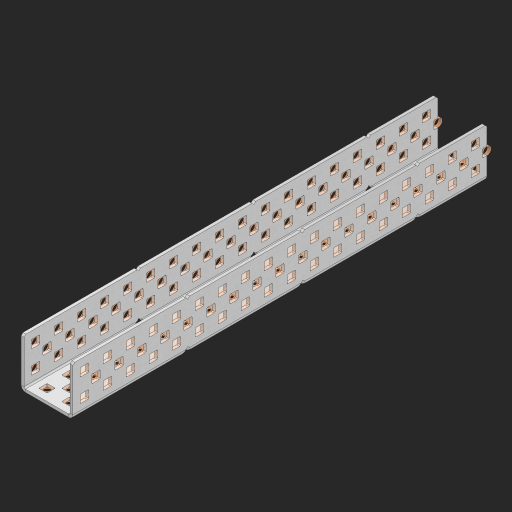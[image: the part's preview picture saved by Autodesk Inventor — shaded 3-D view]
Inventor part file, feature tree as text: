
AUTODESK INVENTOR PART (.ipt)
format: ipt  version: 2023 (Build 270158000, 158)  size: 2,102,784 bytes
history: native  units: in
note: dims shown in document units (in); Inventor stores cm internally (conversion verified against a paired STEP export)
features: other x222, extrude x214, sheet_metal_op x8, sketch x7, mirror x3, pattern_linear x2, chamfer x1
ambient origin geometry x8: Origin, YZ Plane, XZ Plane, XY Plane, X Axis, Y Axis, Z Axis, Center Point
bodies: Solid1 (feature_tree), Body (feature_tree)
feature tree (457):
  sheet_metal_op  "Flanges"
  sheet_metal_op  "Body Pattern"
  pattern_linear  "Center Pattern"  Spacing1=1.0in  [1 undecoded]
  other  "Arc Length"
  mirror  "Notch Mirror"
  pattern_linear  "Notch Pattern"  Spacing1=0.25in  [1 undecoded]
  other  "Diagonal Plane"
  mirror  "Flange 1"
  mirror  "Flange 2"
  chamfer  "End Chamfer"
  sketch  "Sketch1"  dims[d0=1.0in]
  other  "Plate1"
  sketch  "Sketch2"  dims[d1=9.0in]
  other  "Plate2"
  sheet_metal_op  "Bend1"
  sheet_metal_op  "Corner1"
  sketch  "Sketch8"  dims[d2=0.0625in]
  sketch  "Sketch9"  dims[d3=0.0625in]
  other  "Srf91"
  sheet_metal_op  "Body Pattern Sketch"
  other  "Srf92"
  sketch  "Sketch13"  dims[d4=0.0312in]
  sketch  "Sketch15"  dims[d5=0.125in]
  sketch  "Sketch16"  dims[d6=0.0625in d7=1.0in d8=90.0deg d9=0.0312in d10=0.25in d11=0.0625in d12=0.0625in d49=0.182in d50=0.02in d52=0.25in d53=0.0625in d54=0.0in d55=0.172in d56=1.0in d57=0.0in d60=7.0866in d62=0.5in d63=0.7874in d65=0.5in d85=0.1473in d86=0.1782in d88=0.04in d89=0.0625in d90=0.0in d91=0.04in d92=0.0491in d95=2.5in d96=0.04in d97=0.25in d98=45.0deg d99=0.25in d102=2.497in d106=0.182in d107=0.02in d108=0.5in d110=0.0625in d111=0.0in d112=0.172in d113=0.5in d114=0.0in d117=0.5in d118=0.5in d131=0.25in d132=0.25in]
  other  "Srf786"
  other  "Srf889"
  other  "Srf890"
  other  "Srf891"
  other  "Srf892"
  other  "Srf893"
  other  "Srf894"
  other  "Srf895"
  other  "Srf896"
  other  "Srf996"
  other  "Srf997"
  other  "Srf998"
  other  "Srf999"
  other  "Srf1000"
  other  "Srf1255"
  other  "Srf1256"
  other  "Srf1257"
  other  "Srf1258"
  other  "Srf1315"
  other  "Srf1316"
  other  "Srf1317"
  other  "Srf1325"
  other  "Srf1326"
  other  "Srf1327"
  other  "Srf1328"
  other  "Srf1329"
  other  "Srf1330"
  other  "Srf1331"
  other  "Srf1332"
  other  "Srf1338"
  other  "Srf1339"
  other  "Srf1340"
  other  "Srf1341"
  other  "Srf1342"
  other  "Srf1369"
  other  "Srf1370"
  other  "Srf1371"
  other  "Srf1372"
  other  "Srf1374"
  other  "Srf1375"
  other  "Srf1376"
  other  "Srf1384"
  other  "Srf1385"
  other  "Srf1386"
  other  "Srf1387"
  other  "Srf1388"
  other  "Srf1389"
  other  "Srf1390"
  other  "Srf1391"
  other  "Srf1397"
  other  "Srf1398"
  other  "Srf1399"
  other  "Srf1400"
  other  "Srf1401"
  other  "Srf1428"
  other  "Srf1429"
  other  "Srf1430"
  other  "Srf1431"
  other  "Srf1433"
  other  "Srf1434"
  other  "Srf1473"
  other  "Srf1474"
  other  "Srf1475"
  other  "Srf1476"
  other  "Srf1477"
  other  "Srf1478"
  other  "Srf1479"
  other  "Srf1480"
  other  "Srf1481"
  other  "Srf1482"
  other  "Srf1483"
  other  "Srf1484"
  other  "Srf1485"
  other  "Srf1486"
  other  "Srf1487"
  other  "Srf1488"
  other  "Srf1489"
  other  "Srf1490"
  other  "Srf1500"
  other  "Srf1501"
  other  "Srf1502"
  other  "Srf1503"
  other  "Srf1504"
  other  "Srf1505"
  other  "Srf1506"
  other  "Srf1507"
  other  "Srf1508"
  other  "Srf1509"
  other  "Srf1510"
  other  "Srf1511"
  other  "Srf1512"
  other  "Srf1513"
  other  "Srf1514"
  other  "Srf1515"
  other  "Srf1516"
  other  "Srf1517"
  other  "Srf1518"
  other  "Srf1519"
  other  "Srf1520"
  other  "Srf1521"
  other  "Srf1522"
  other  "Srf1523"
  other  "Srf1524"
  other  "Srf1525"
  other  "Srf1526"
  other  "Srf1527"
  other  "Srf1528"
  other  "Srf1529"
  other  "Srf1530"
  other  "Srf1531"
  other  "Srf1532"
  other  "Srf1533"
  other  "Srf1538"
  other  "Srf1539"
  other  "Srf1540"
  other  "Srf1541"
  other  "Srf1542"
  other  "Srf1543"
  other  "Srf1544"
  other  "Srf1545"
  other  "Srf1546"
  other  "Srf1547"
  other  "Srf1548"
  other  "Srf1549"
  other  "Srf1550"
  other  "Srf1551"
  other  "Srf1552"
  other  "Srf1553"
  other  "Srf1554"
  other  "Srf1555"
  other  "Srf1556"
  other  "Srf1557"
  other  "Srf1558"
  other  "Srf1559"
  other  "Srf1560"
  other  "Srf1561"
  other  "Srf1562"
  other  "Srf1563"
  other  "Srf1564"
  other  "Srf1565"
  other  "Srf1566"
  other  "Srf1567"
  other  "Srf1568"
  other  "Srf1569"
  other  "Srf1570"
  other  "Srf1571"
  other  "Srf1576"
  other  "Srf1577"
  other  "Srf1578"
  other  "Srf1579"
  other  "Srf1580"
  other  "Srf1581"
  other  "Srf1582"
  other  "Srf1583"
  other  "Srf1584"
  other  "Srf1585"
  other  "Srf1586"
  other  "Srf1587"
  other  "Srf1588"
  other  "Srf1589"
  other  "Srf1590"
  other  "Srf1591"
  other  "Srf1592"
  other  "Srf1593"
  other  "Srf1594"
  other  "Srf1595"
  other  "Srf1596"
  other  "Srf1597"
  other  "Srf1598"
  other  "Srf1599"
  other  "Srf1600"
  other  "Srf1601"
  other  "Srf1602"
  other  "Srf1603"
  other  "Srf1604"
  other  "Srf1605"
  other  "Srf1606"
  other  "Srf1607"
  other  "Srf1608"
  other  "Srf1609"
  other  "Srf1614"
  other  "Srf1615"
  other  "Srf1616"
  other  "Srf1617"
  other  "Srf1618"
  other  "Srf1619"
  other  "Srf1620"
  other  "Srf1621"
  other  "Srf1622"
  other  "Srf1623"
  other  "Srf1624"
  other  "Srf1625"
  other  "Srf1626"
  other  "Srf1627"
  other  "Srf1628"
  other  "Srf1629"
  other  "Srf1630"
  other  "Srf1631"
  other  "Srf1632"
  other  "Srf1633"
  other  "Srf1634"
  other  "Srf1635"
  other  "Srf1636"
  other  "Srf1637"
  other  "Srf1638"
  other  "Srf1639"
  other  "Srf1640"
  other  "Srf1641"
  other  "Srf1642"
  other  "Srf1643"
  other  "Srf1644"
  other  "Srf1645"
  other  "Srf1646"
  other  "Srf1647"
  sheet_metal_op  "Body Stamp"
  sheet_metal_op  "Body Circle"
  other  "Center Stamp"
  other  "Center Circle"
  sheet_metal_op  "Notch"
  extrude  "ExtrusionSrf92"  Depth=0.0625in
  extrude  "ExtrusionSrf889"  Depth=0.0625in
  extrude  "ExtrusionSrf890"  Depth=0.182in
  extrude  "ExtrusionSrf891"  Depth=0.02in
  extrude  "ExtrusionSrf892"  Depth=0.25in
  extrude  "ExtrusionSrf893"  Depth=0.0625in
  extrude  "ExtrusionSrf894"  TaperAngle=0.0deg  [1 undecoded]
  extrude  "ExtrusionSrf895"  Depth=0.25in
  extrude  "ExtrusionSrf896"  Depth=1.0in TaperAngle=0.0deg
  extrude  "ExtrusionSrf996"  Depth=0.25in
  extrude  "ExtrusionSrf997"  Depth=0.5in
  extrude  "ExtrusionSrf998"  Depth=0.25in
  extrude  "ExtrusionSrf999"  Depth=0.25in
  extrude  "ExtrusionSrf1000"  Depth=0.25in
  extrude  "ExtrusionSrf1255"  Depth=0.0625in
  extrude  "ExtrusionSrf1256"  TaperAngle=0.0deg  [1 undecoded]
  extrude  "ExtrusionSrf1257"  Depth=0.25in
  extrude  "ExtrusionSrf1258"  Depth=0.25in
  extrude  "ExtrusionSrf1315"  Depth=2.5in
  extrude  "ExtrusionSrf1316"  Depth=0.25in TaperAngle=45.0deg
  extrude  "ExtrusionSrf1355"  Depth=0.25in
  extrude  "ExtrusionSrf1356"  Depth=0.25in
  extrude  "ExtrusionSrf1357"  Depth=0.182in
  extrude  "ExtrusionSrf1358"  Depth=0.02in
  extrude  "ExtrusionSrf1359"  Depth=0.5in
  extrude  "ExtrusionSrf1360"  Depth=0.0625in
  extrude  "ExtrusionSrf1361"  TaperAngle=0.0deg  [1 undecoded]
  extrude  "ExtrusionSrf1362"  Depth=0.25in
  extrude  "ExtrusionSrf1363"  Depth=0.5in TaperAngle=0.0deg
  extrude  "ExtrusionSrf1364"  Depth=0.5in
  extrude  "ExtrusionSrf1365"  Depth=0.5in
  extrude  "ExtrusionSrf1366"  Depth=0.25in
  extrude  "ExtrusionSrf1367"  Depth=0.25in
  extrude  "ExtrusionSrf1368"  [1 undecoded]
  extrude  "ExtrusionSrf1369"  [1 undecoded]
  extrude  "ExtrusionSrf1370"  [1 undecoded]
  extrude  "ExtrusionSrf1371"  [1 undecoded]
  extrude  "ExtrusionSrf1372"  [1 undecoded]
  extrude  "ExtrusionSrf1374"  [1 undecoded]
  extrude  "ExtrusionSrf1375"  [1 undecoded]
  extrude  "ExtrusionSrf1414"  [1 undecoded]
  extrude  "ExtrusionSrf1415"  [1 undecoded]
  extrude  "ExtrusionSrf1416"  [1 undecoded]
  extrude  "ExtrusionSrf1417"  [1 undecoded]
  extrude  "ExtrusionSrf1418"  [1 undecoded]
  extrude  "ExtrusionSrf1419"  [1 undecoded]
  extrude  "ExtrusionSrf1420"  [1 undecoded]
  extrude  "ExtrusionSrf1421"  [1 undecoded]
  extrude  "ExtrusionSrf1422"  [1 undecoded]
  extrude  "ExtrusionSrf1423"  [1 undecoded]
  extrude  "ExtrusionSrf1424"  [1 undecoded]
  extrude  "ExtrusionSrf1425"  [1 undecoded]
  extrude  "ExtrusionSrf1426"  [1 undecoded]
  extrude  "ExtrusionSrf1427"  [1 undecoded]
  extrude  "ExtrusionSrf1428"  [1 undecoded]
  extrude  "ExtrusionSrf1429"  [1 undecoded]
  extrude  "ExtrusionSrf1430"  [1 undecoded]
  extrude  "ExtrusionSrf1431"  [1 undecoded]
  extrude  "ExtrusionSrf1433"  [1 undecoded]
  extrude  "ExtrusionSrf1434"  [1 undecoded]
  extrude  "ExtrusionSrf1473"  [1 undecoded]
  extrude  "ExtrusionSrf1474"  [1 undecoded]
  extrude  "ExtrusionSrf1475"  [1 undecoded]
  extrude  "ExtrusionSrf1476"  [1 undecoded]
  extrude  "ExtrusionSrf1477"  [1 undecoded]
  extrude  "ExtrusionSrf1478"  [1 undecoded]
  extrude  "ExtrusionSrf1479"  [1 undecoded]
  extrude  "ExtrusionSrf1480"  [1 undecoded]
  extrude  "ExtrusionSrf1481"  [1 undecoded]
  extrude  "ExtrusionSrf1482"  [1 undecoded]
  extrude  "ExtrusionSrf1483"  [1 undecoded]
  extrude  "ExtrusionSrf1484"  [1 undecoded]
  extrude  "ExtrusionSrf1485"  [1 undecoded]
  extrude  "ExtrusionSrf1486"  [1 undecoded]
  extrude  "ExtrusionSrf1487"  [1 undecoded]
  extrude  "ExtrusionSrf1488"  [1 undecoded]
  extrude  "ExtrusionSrf1489"  [1 undecoded]
  extrude  "ExtrusionSrf1490"  [1 undecoded]
  extrude  "ExtrusionSrf1500"  [1 undecoded]
  extrude  "ExtrusionSrf1501"  [1 undecoded]
  extrude  "ExtrusionSrf1502"  [1 undecoded]
  extrude  "ExtrusionSrf1503"  [1 undecoded]
  extrude  "ExtrusionSrf1504"  [1 undecoded]
  extrude  "ExtrusionSrf1505"  [1 undecoded]
  extrude  "ExtrusionSrf1506"  [1 undecoded]
  extrude  "ExtrusionSrf1507"  [1 undecoded]
  extrude  "ExtrusionSrf1508"  [1 undecoded]
  extrude  "ExtrusionSrf1509"  [1 undecoded]
  extrude  "ExtrusionSrf1510"  [1 undecoded]
  extrude  "ExtrusionSrf1511"  [1 undecoded]
  extrude  "ExtrusionSrf1512"  [1 undecoded]
  extrude  "ExtrusionSrf1513"  [1 undecoded]
  extrude  "ExtrusionSrf1514"  [1 undecoded]
  extrude  "ExtrusionSrf1515"  [1 undecoded]
  extrude  "ExtrusionSrf1516"  [1 undecoded]
  extrude  "ExtrusionSrf1517"  [1 undecoded]
  extrude  "ExtrusionSrf1518"  [1 undecoded]
  extrude  "ExtrusionSrf1519"  [1 undecoded]
  extrude  "ExtrusionSrf1520"  [1 undecoded]
  extrude  "ExtrusionSrf1521"  [1 undecoded]
  extrude  "ExtrusionSrf1522"  [1 undecoded]
  extrude  "ExtrusionSrf1523"  [1 undecoded]
  extrude  "ExtrusionSrf1524"  [1 undecoded]
  extrude  "ExtrusionSrf1525"  [1 undecoded]
  extrude  "ExtrusionSrf1526"  [1 undecoded]
  extrude  "ExtrusionSrf1527"  [1 undecoded]
  extrude  "ExtrusionSrf1528"  [1 undecoded]
  extrude  "ExtrusionSrf1529"  [1 undecoded]
  extrude  "ExtrusionSrf1530"  [1 undecoded]
  extrude  "ExtrusionSrf1531"  [1 undecoded]
  extrude  "ExtrusionSrf1532"  [1 undecoded]
  extrude  "ExtrusionSrf1533"  [1 undecoded]
  extrude  "ExtrusionSrf1538"  [1 undecoded]
  extrude  "ExtrusionSrf1539"  [1 undecoded]
  extrude  "ExtrusionSrf1540"  [1 undecoded]
  extrude  "ExtrusionSrf1541"  [1 undecoded]
  extrude  "ExtrusionSrf1542"  [1 undecoded]
  extrude  "ExtrusionSrf1543"  [1 undecoded]
  extrude  "ExtrusionSrf1544"  [1 undecoded]
  extrude  "ExtrusionSrf1545"  [1 undecoded]
  extrude  "ExtrusionSrf1546"  [1 undecoded]
  extrude  "ExtrusionSrf1547"  [1 undecoded]
  extrude  "ExtrusionSrf1548"  [1 undecoded]
  extrude  "ExtrusionSrf1549"  [1 undecoded]
  extrude  "ExtrusionSrf1550"  [1 undecoded]
  extrude  "ExtrusionSrf1551"  [1 undecoded]
  extrude  "ExtrusionSrf1552"  [1 undecoded]
  extrude  "ExtrusionSrf1553"  [1 undecoded]
  extrude  "ExtrusionSrf1554"  [1 undecoded]
  extrude  "ExtrusionSrf1555"  [1 undecoded]
  extrude  "ExtrusionSrf1556"  [1 undecoded]
  extrude  "ExtrusionSrf1557"  [1 undecoded]
  extrude  "ExtrusionSrf1558"  [1 undecoded]
  extrude  "ExtrusionSrf1559"  [1 undecoded]
  extrude  "ExtrusionSrf1560"  [1 undecoded]
  extrude  "ExtrusionSrf1561"  [1 undecoded]
  extrude  "ExtrusionSrf1562"  [1 undecoded]
  extrude  "ExtrusionSrf1563"  [1 undecoded]
  extrude  "ExtrusionSrf1564"  [1 undecoded]
  extrude  "ExtrusionSrf1565"  [1 undecoded]
  extrude  "ExtrusionSrf1566"  [1 undecoded]
  extrude  "ExtrusionSrf1567"  [1 undecoded]
  extrude  "ExtrusionSrf1568"  [1 undecoded]
  extrude  "ExtrusionSrf1569"  [1 undecoded]
  extrude  "ExtrusionSrf1570"  [1 undecoded]
  extrude  "ExtrusionSrf1571"  [1 undecoded]
  extrude  "ExtrusionSrf1576"  [1 undecoded]
  extrude  "ExtrusionSrf1577"  [1 undecoded]
  extrude  "ExtrusionSrf1578"  [1 undecoded]
  extrude  "ExtrusionSrf1579"  [1 undecoded]
  extrude  "ExtrusionSrf1580"  [1 undecoded]
  extrude  "ExtrusionSrf1581"  [1 undecoded]
  extrude  "ExtrusionSrf1582"  [1 undecoded]
  extrude  "ExtrusionSrf1583"  [1 undecoded]
  extrude  "ExtrusionSrf1584"  [1 undecoded]
  extrude  "ExtrusionSrf1585"  [1 undecoded]
  extrude  "ExtrusionSrf1586"  [1 undecoded]
  extrude  "ExtrusionSrf1587"  [1 undecoded]
  extrude  "ExtrusionSrf1588"  [1 undecoded]
  extrude  "ExtrusionSrf1589"  [1 undecoded]
  extrude  "ExtrusionSrf1590"  [1 undecoded]
  extrude  "ExtrusionSrf1591"  [1 undecoded]
  extrude  "ExtrusionSrf1592"  [1 undecoded]
  extrude  "ExtrusionSrf1593"  [1 undecoded]
  extrude  "ExtrusionSrf1594"  [1 undecoded]
  extrude  "ExtrusionSrf1595"  [1 undecoded]
  extrude  "ExtrusionSrf1596"  [1 undecoded]
  extrude  "ExtrusionSrf1597"  [1 undecoded]
  extrude  "ExtrusionSrf1598"  [1 undecoded]
  extrude  "ExtrusionSrf1599"  [1 undecoded]
  extrude  "ExtrusionSrf1600"  [1 undecoded]
  extrude  "ExtrusionSrf1601"  [1 undecoded]
  extrude  "ExtrusionSrf1602"  [1 undecoded]
  extrude  "ExtrusionSrf1603"  [1 undecoded]
  extrude  "ExtrusionSrf1604"  [1 undecoded]
  extrude  "ExtrusionSrf1605"  [1 undecoded]
  extrude  "ExtrusionSrf1606"  [1 undecoded]
  extrude  "ExtrusionSrf1607"  [1 undecoded]
  extrude  "ExtrusionSrf1608"  [1 undecoded]
  extrude  "ExtrusionSrf1609"  [1 undecoded]
  extrude  "ExtrusionSrf1614"  [1 undecoded]
  extrude  "ExtrusionSrf1615"  [1 undecoded]
  extrude  "ExtrusionSrf1616"  [1 undecoded]
  extrude  "ExtrusionSrf1617"  [1 undecoded]
  extrude  "ExtrusionSrf1618"  [1 undecoded]
  extrude  "ExtrusionSrf1619"  [1 undecoded]
  extrude  "ExtrusionSrf1620"  [1 undecoded]
  extrude  "ExtrusionSrf1621"  [1 undecoded]
  extrude  "ExtrusionSrf1622"  [1 undecoded]
  extrude  "ExtrusionSrf1623"  [1 undecoded]
  extrude  "ExtrusionSrf1624"  [1 undecoded]
  extrude  "ExtrusionSrf1625"  [1 undecoded]
  extrude  "ExtrusionSrf1626"  [1 undecoded]
  extrude  "ExtrusionSrf1627"  [1 undecoded]
  extrude  "ExtrusionSrf1628"  [1 undecoded]
  extrude  "ExtrusionSrf1629"  [1 undecoded]
  extrude  "ExtrusionSrf1630"  [1 undecoded]
  extrude  "ExtrusionSrf1631"  [1 undecoded]
  extrude  "ExtrusionSrf1632"  [1 undecoded]
  extrude  "ExtrusionSrf1633"  [1 undecoded]
  extrude  "ExtrusionSrf1634"  [1 undecoded]
  extrude  "ExtrusionSrf1635"  [1 undecoded]
  extrude  "ExtrusionSrf1636"  [1 undecoded]
  extrude  "ExtrusionSrf1637"  [1 undecoded]
  extrude  "ExtrusionSrf1638"  [1 undecoded]
  extrude  "ExtrusionSrf1639"  [1 undecoded]
  extrude  "ExtrusionSrf1640"  [1 undecoded]
  extrude  "ExtrusionSrf1641"  [1 undecoded]
  extrude  "ExtrusionSrf1642"  [1 undecoded]
  extrude  "ExtrusionSrf1643"  [1 undecoded]
  extrude  "ExtrusionSrf1644"  [1 undecoded]
  extrude  "ExtrusionSrf1645"  [1 undecoded]
  extrude  "ExtrusionSrf1646"  [1 undecoded]
  extrude  "ExtrusionSrf1647"  [1 undecoded]
note: 186 required parameter values undecoded (feature->parameter linkage not recoverable at this tier; creation-order binding heuristic only, values carry confidence <= 0.55)
